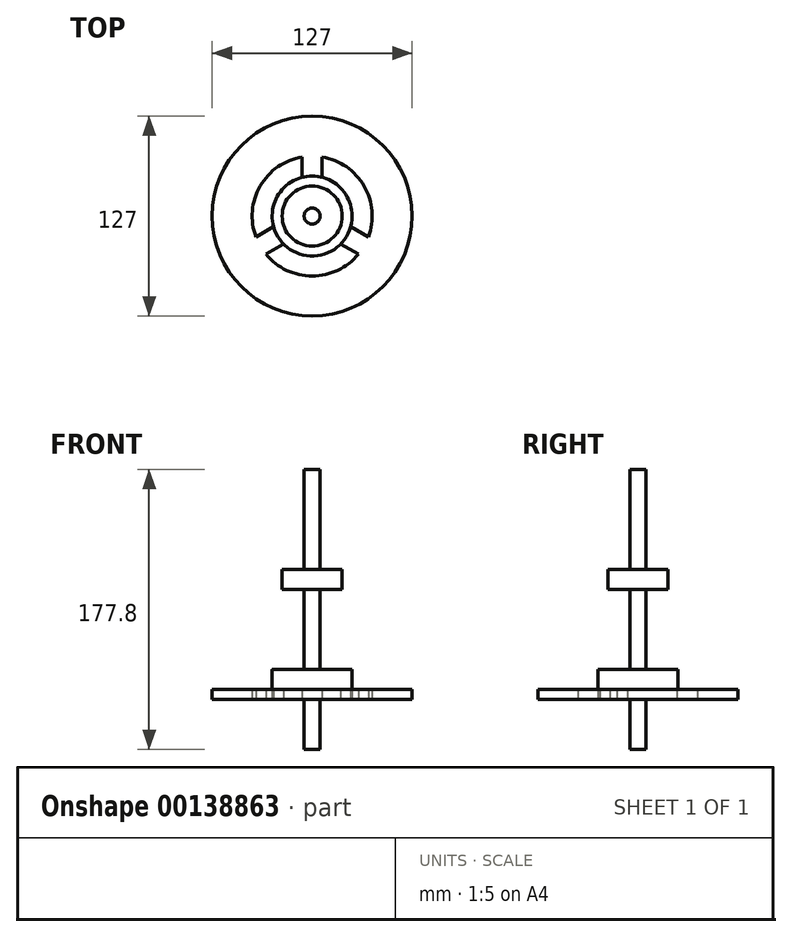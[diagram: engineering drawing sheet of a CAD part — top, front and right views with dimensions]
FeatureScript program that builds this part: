
annotation { "Feature Type Name" : "Feature", "Feature Type Description" : "" }
export const myFeature = defineFeature(function(context is Context, id is Id, definition is map)
    precondition{}
    {
        {
            var Q0;
            Q0=qCreatedBy(makeId("Top.planeOp"),FACE);
            var sketch = newSketch(context, id + "F0", { "sketchPlane" : qUnion([Q0])});
            skCircle(sketch, "E0", {"center": v(0, 0) * mm, "radius": 63.5 * mm});
            skCircle(sketch, "E1", {"center": v(0, 0) * mm, "radius": 38.1 * mm});
            skSolve(sketch);
        }
        {
            var Q0;
            Q0=qSketchRegion(id+"F0",true);
            extrude(context, id + "F1", {"entities" : qUnion([Q0]), "depth" : 6.35 * mm});
        }
        {
            var Q0;
            Q0=qCreatedBy(makeId("Top.planeOp"),FACE);
            var sketch = newSketch(context, id + "F2", { "sketchPlane" : qUnion([Q0])});
            skCircle(sketch, "E2.0", {"center": v(0, 0) * mm, "radius": 50.8 * mm});
            skCircle(sketch, "E2.1", {"center": v(0, 0) * mm, "radius": 25.4 * mm});
            skLineSegment(sketch, "E3.1.0", {"start": v(-6.35, 50.4) * mm, "end": v(-6.35, 24.6) * mm});
            skLineSegment(sketch, "E3.1.1", {"start": v(6.35, 50.4) * mm, "end": v(6.35, 24.6) * mm});
            skLineSegment(sketch, "E4.1.0", {"start": v(-40.47, -30.7) * mm, "end": v(-18.12, -17.8) * mm});
            skLineSegment(sketch, "E4.1.1", {"start": v(-46.82, -19.7) * mm, "end": v(-24.47, -6.8) * mm});
            skLineSegment(sketch, "E4.2.0", {"start": v(46.82, -19.7) * mm, "end": v(24.47, -6.8) * mm});
            skLineSegment(sketch, "E4.2.1", {"start": v(40.47, -30.7) * mm, "end": v(18.12, -17.8) * mm});
            skSolve(sketch);
        }
        {
            var Q0;
            Q0=qCreatedBy(makeId("Top.planeOp"),FACE);
            var sketch = newSketch(context, id + "F3", { "sketchPlane" : qUnion([Q0])});
            skCircle(sketch, "E5", {"center": v(0, 0) * mm, "radius": 25.4 * mm});
            skSolve(sketch);
        }
        {
            var Q0;
            {var subQ0=sQuery(id+"F2.wireOp",EDGE,"E2.1");var subQ4=makeQuery(id+"F2.imprint","INTERSECT",VERTEX,{"derivedFrom":[subQ0,sQuery(id+"F2.wireOp",EDGE,"E3.1.0")]});Q0=makeQuery(id+"F2.imprint","IMPRINT",FACE,{"disambiguationData":[TD([[makeQuery(id+"F2.imprint","IMPRINT",EDGE,{"disambiguationData":[TD([[subQ4,1.0]])],"derivedFrom":subQ0}),1.0]])]});}
            var Q1;
            {var subQ0=sQuery(id+"F2.wireOp",EDGE,"E4.1.0");Q1=makeQuery(id+"F2.imprint","IMPRINT",FACE,{"disambiguationData":[TD([[makeQuery(id+"F2.imprint","IMPRINT",EDGE,{"derivedFrom":subQ0}),1.0]])]});}
            var Q2;
            {var subQ0=sQuery(id+"F2.wireOp",EDGE,"E3.1.0");Q2=makeQuery(id+"F2.imprint","IMPRINT",FACE,{"disambiguationData":[TD([[makeQuery(id+"F2.imprint","IMPRINT",EDGE,{"derivedFrom":subQ0}),1.0]])]});}
            var Q3;
            {var subQ0=sQuery(id+"F2.wireOp",EDGE,"E4.2.0");Q3=makeQuery(id+"F2.imprint","IMPRINT",FACE,{"disambiguationData":[TD([[makeQuery(id+"F2.imprint","IMPRINT",EDGE,{"derivedFrom":subQ0}),1.0]])]});}
            var Q4;
            Q4=makeQuery(id+"F1.opExtrude","CAP_FACE",FACE,{"disambiguationData":[OSD([sQuery(id+"F0.wireOp",EDGE,"E0"),sQuery(id+"F0.wireOp",EDGE,"E1")])],"isStart":false});
            extrude(context, id + "F4", {"entities" : qUnion([Q0, Q1, Q2, Q3]), "operationType" : NewBodyOperationType.ADD, "endBound" : BoundingType.UP_TO_SURFACE, "endBoundEntityFace" : qUnion([Q4]), "depth" : 25.4 * mm});
        }
        {
            var Q0;
            {var subQ0=sQuery(id+"F0.wireOp",EDGE,"E1");var subQ1=sQuery(id+"F0.wireOp",EDGE,"E0");Q0=makeQuery(id+"F4.boolean.opBoolean","MERGE",FACE,{"derivedFrom":[makeQuery(id+"F1.opExtrude","CAP_FACE",FACE,{"disambiguationData":[OSD([subQ1,subQ0])],"isStart":false}),makeQuery(id+"F4.opExtrude","CAP_FACE",FACE,{"disambiguationData":[OSD([subQ1,subQ0])],"isStart":false})]});}
            var sketch = newSketch(context, id + "F5", { "sketchPlane" : qUnion([Q0])});
            skCircle(sketch, "E6.0", {"center": v(0, 0) * mm, "radius": 25.4 * mm});
            skSolve(sketch);
        }
        {
            var Q0;
            Q0=qSketchRegion(id+"F5",true);
            extrude(context, id + "F6", {"entities" : qUnion([Q0]), "operationType" : NewBodyOperationType.ADD, "depth" : 12.7 * mm});
        }
        {
            var Q0;
            Q0=makeQuery(id+"F6.opExtrude","CAP_FACE",FACE,{"disambiguationData":[OSD([sQuery(id+"F5.wireOp",EDGE,"E6.0")])],"isStart":false});
            var sketch = newSketch(context, id + "F7", { "sketchPlane" : qUnion([Q0])});
            skCircle(sketch, "E7", {"center": v(0, 0) * mm, "radius": 5.08 * mm});
            skSolve(sketch);
        }
        {
            var Q0;
            Q0=qSketchRegion(id+"F7",true);
            var Q1;
            Q1=makeQuery(id+"F4.boolean.opBoolean","MERGE",FACE,{"derivedFrom":[makeQuery(id+"F1.opExtrude","CAP_FACE",FACE,{"disambiguationData":[OSD([sQuery(id+"F0.wireOp",EDGE,"E0"),sQuery(id+"F0.wireOp",EDGE,"E1")])],"isStart":true}),makeQuery(id+"F4.opExtrude","CAP_FACE",FACE,{"disambiguationData":[OSD([sQuery(id+"F2.wireOp",EDGE,"E2.0"),sQuery(id+"F2.wireOp",EDGE,"E2.1"),sQuery(id+"F2.wireOp",EDGE,"E3.1.0"),sQuery(id+"F2.wireOp",EDGE,"E3.1.1"),sQuery(id+"F2.wireOp",EDGE,"E4.1.0"),sQuery(id+"F2.wireOp",EDGE,"E4.1.1"),sQuery(id+"F2.wireOp",EDGE,"E4.2.0"),sQuery(id+"F2.wireOp",EDGE,"E4.2.1")])],"isStart":true})]});
            extrude(context, id + "F8", {"entities" : qUnion([Q0]), "operationType" : NewBodyOperationType.ADD, "oppositeDirection" : true, "endBoundEntityFace" : qUnion([Q1]), "depth" : 50.8 * mm});
        }
        {
            var Q0;
            Q0=makeQuery(id+"F6.opExtrude","CAP_FACE",FACE,{"disambiguationData":[OSD([sQuery(id+"F5.wireOp",EDGE,"E6.0")])],"isStart":false});
            var sketch = newSketch(context, id + "F9", { "sketchPlane" : qUnion([Q0])});
            skCircle(sketch, "E8.0", {"center": v(0, 0) * mm, "radius": 5.08 * mm});
            skCircle(sketch, "E8.2", {"center": v(0, 0) * mm, "radius": 25.4 * mm, "construction": true});
            skPoint(sketch, "E8.3", {"position": v(0, 0) * mm});
            skSolve(sketch);
        }
        {
            var Q0;
            Q0=qSketchRegion(id+"F9",true);
            extrude(context, id + "F10", {"entities" : qUnion([Q0]), "operationType" : NewBodyOperationType.ADD, "depth" : 127 * mm});
        }
        {
            var Q0;
            Q0=qCreatedBy(makeId("Front.planeOp"),FACE);
            var sketch = newSketch(context, id + "F11", { "sketchPlane" : qUnion([Q0])});
            skLineSegment(sketch, "E9", {"start": v(0, 0) * mm, "end": v(0, 69.85) * mm, "construction": true});
            skSolve(sketch);
        }
        {
            var Q0;
            Q0=qCreatedBy(makeId("Top.planeOp"),FACE);
            var Q1;
            Q1=sQuery(id+"F11.wireOp",VERTEX,"E9.end");
            cPlane(context, id + "F12", {"entities" : qUnion([Q0, Q1]), "cplaneType" : CPlaneType.PLANE_POINT, "offset" : 25.4 * mm, "width" : 152.4 * mm, "height" : 152.4 * mm});
        }
        {
            var Q0;
            Q0=qCreatedBy(id+"F12.planeOp",FACE);
            var sketch = newSketch(context, id + "F13", { "sketchPlane" : qUnion([Q0])});
            skCircle(sketch, "E10", {"center": v(0, 0) * mm, "radius": 19.05 * mm});
            skSolve(sketch);
        }
        {
            var Q0;
            Q0=qSketchRegion(id+"F13",true);
            extrude(context, id + "F14", {"entities" : qUnion([Q0]), "operationType" : NewBodyOperationType.ADD, "depth" : 12.7 * mm});
        }
    });
